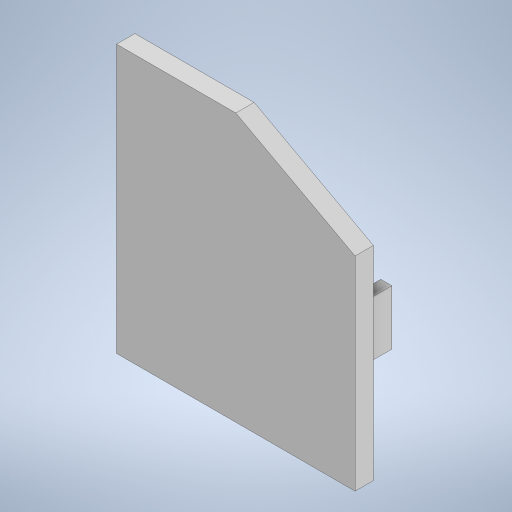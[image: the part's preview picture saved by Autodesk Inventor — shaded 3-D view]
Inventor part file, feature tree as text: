
AUTODESK INVENTOR PART (.ipt)
format: ipt  version: 2024 (Build 280153000, 153)  size: 240,640 bytes
history: native  units: mm
features: extrude x2, sketch x2, projected_geometry x1
ambient origin geometry x8: Origin, YZ Plane, XZ Plane, XY Plane, X Axis, Y Axis, Z Axis, Center Point
bodies: Solid1 (feature_tree)
feature tree (5):
  extrude  "Extrusion1"  Depth=146.0mm
  extrude  "Extrusion2"  Depth=12.0mm
  sketch  "Sketch1"  dims[d0=65.0mm d1=146.0mm]
  sketch  "Sketch2"  dims[d2=65.0mm d3=111.0mm d4=65.0mm d5=10.0mm d6=0.0mm d7=10.0mm d8=10.0mm d9=10.0mm d10=70.0mm d11=2.0mm d12=15.0mm d13=6.0mm d14=30.0mm d15=70.0mm d16=2.0mm d17=15.0mm d18=6.0mm d19=30.0mm d20=2.0mm d21=20.0mm d22=6.0mm d23=40.0mm d24=12.0mm d25=0.0mm]
  projected_geometry  "Projected Loop1"
